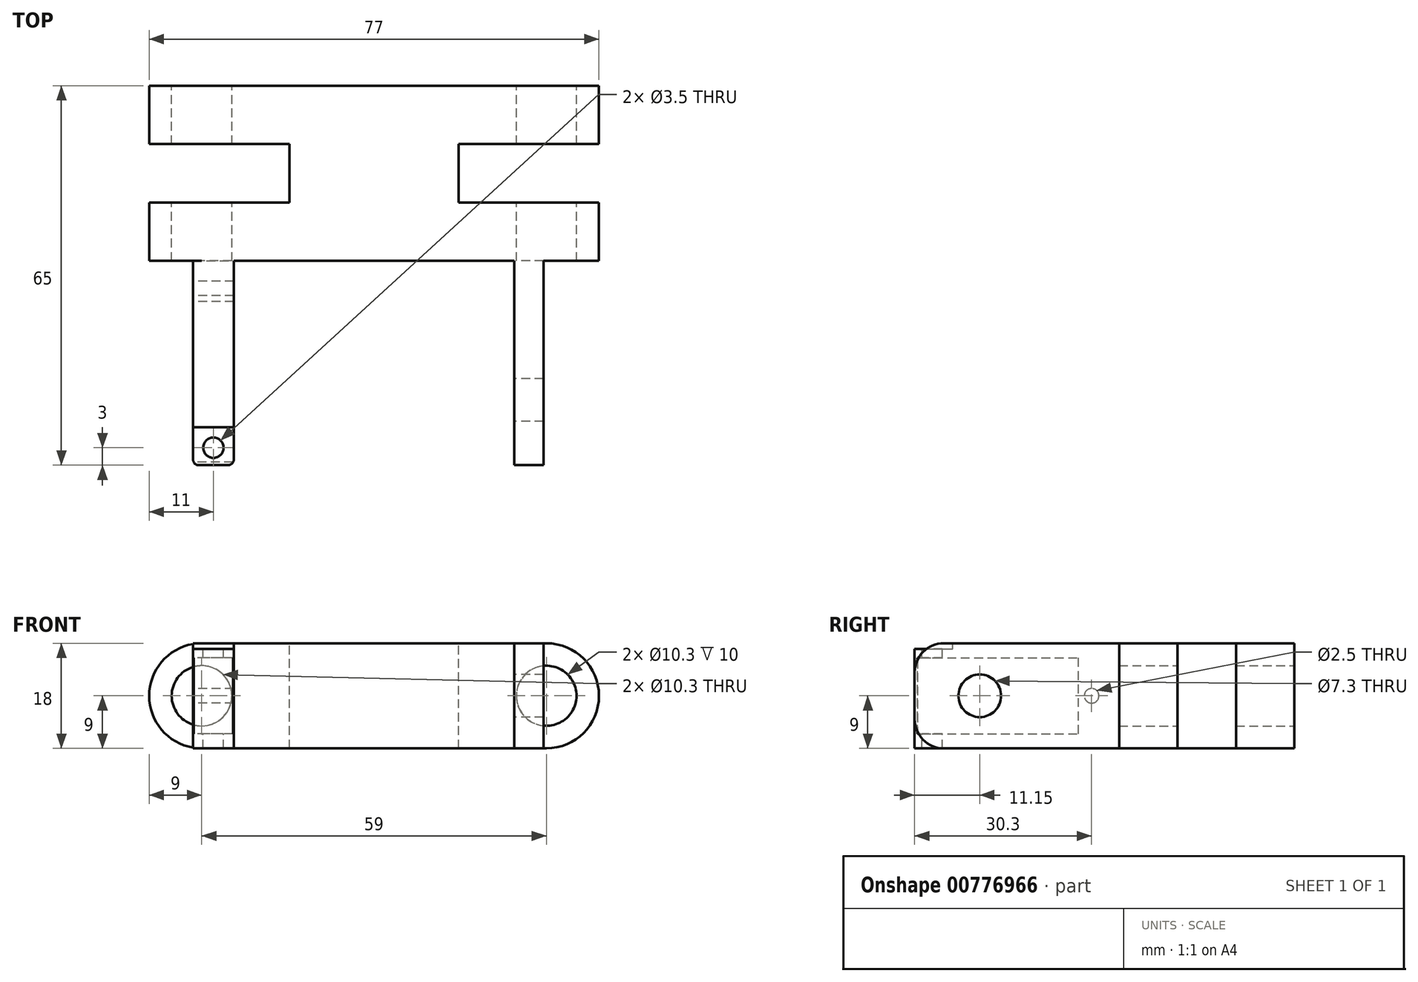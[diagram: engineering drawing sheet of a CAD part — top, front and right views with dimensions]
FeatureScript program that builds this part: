
annotation { "Feature Type Name" : "Feature", "Feature Type Description" : "" }
export const myFeature = defineFeature(function(context is Context, id is Id, definition is map)
    precondition{}
    {
        {
            var Q0;
            Q0=qCreatedBy(makeId("Front.planeOp"),FACE);
            var sketch = newSketch(context, id + "F0", { "sketchPlane" : qUnion([Q0])});
            skCircle(sketch, "E0", {"center": v(-59, 0) * mm, "radius": 5.15 * mm});
            skCircle(sketch, "E1", {"center": v(0, 0) * mm, "radius": 5.15 * mm});
            skCircle(sketch, "E2", {"center": v(-59, 0) * mm, "radius": 9 * mm});
            skCircle(sketch, "E3", {"center": v(0, 0) * mm, "radius": 9 * mm});
            skLineSegment(sketch, "E4", {"start": v(-59, 9) * mm, "end": v(0, 9) * mm});
            skLineSegment(sketch, "E5", {"start": v(-59, -9) * mm, "end": v(0, -9) * mm});
            skSolve(sketch);
        }
        {
            var Q0;
            Q0=qSketchRegion(id+"F0",true);
            extrude(context, id + "F1", {"entities" : qUnion([Q0]), "depth" : 30 * mm});
        }
        {
            var Q0;
            Q0=makeQuery(id+"F1.opExtrude","SWEPT_FACE",FACE,{"disambiguationData":[OSD([sQuery(id+"F0.wireOp",EDGE,"E4")])]});
            var sketch = newSketch(context, id + "F2", { "sketchPlane" : qUnion([Q0])});
            skLineSegment(sketch, "E6.bottom", {"start": v(-15, -10) * mm, "end": v(11.25, -10) * mm});
            skLineSegment(sketch, "E6.top", {"start": v(-15, -20) * mm, "end": v(11.25, -20) * mm});
            skLineSegment(sketch, "E6.left", {"start": v(-15, -10) * mm, "end": v(-15, -20) * mm});
            skLineSegment(sketch, "E6.right", {"start": v(11.25, -10) * mm, "end": v(11.25, -20) * mm});
            skLineSegment(sketch, "E7.bottom", {"start": v(-44, -10) * mm, "end": v(-74.23, -10) * mm});
            skLineSegment(sketch, "E7.top", {"start": v(-44, -20) * mm, "end": v(-74.23, -20) * mm});
            skLineSegment(sketch, "E7.left", {"start": v(-44, -10) * mm, "end": v(-44, -20) * mm});
            skLineSegment(sketch, "E7.right", {"start": v(-74.23, -10) * mm, "end": v(-74.23, -20) * mm});
            skSolve(sketch);
        }
        {
            var Q0;
            Q0=qSketchRegion(id+"F2",true);
            extrude(context, id + "F3", {"entities" : qUnion([Q0]), "operationType" : NewBodyOperationType.REMOVE, "oppositeDirection" : true, "depth" : 25 * mm});
        }
        {
            var Q0;
            Q0=makeQuery(id+"F1.opExtrude","CAP_FACE",FACE,{"disambiguationData":[OSD([sQuery(id+"F0.wireOp",EDGE,"E0"),sQuery(id+"F0.wireOp",EDGE,"E1"),sQuery(id+"F0.wireOp",EDGE,"E2"),sQuery(id+"F0.wireOp",EDGE,"E3"),sQuery(id+"F0.wireOp",EDGE,"E4"),sQuery(id+"F0.wireOp",EDGE,"E5")])],"isStart":false});
            var sketch = newSketch(context, id + "F4", { "sketchPlane" : qUnion([Q0])});
            skLineSegment(sketch, "E8.bottom", {"start": v(-5.5, 9) * mm, "end": v(-0.5, 9) * mm});
            skLineSegment(sketch, "E8.top", {"start": v(-5.5, -9) * mm, "end": v(-0.5, -9) * mm});
            skLineSegment(sketch, "E8.left", {"start": v(-5.5, 9) * mm, "end": v(-5.5, -9) * mm});
            skLineSegment(sketch, "E8.right", {"start": v(-0.5, 9) * mm, "end": v(-0.5, -9) * mm});
            skLineSegment(sketch, "E9.bottom", {"start": v(-60.5, 9) * mm, "end": v(-53.5, 9) * mm});
            skLineSegment(sketch, "E9.top", {"start": v(-60.5, -9) * mm, "end": v(-53.5, -9) * mm});
            skLineSegment(sketch, "E9.left", {"start": v(-60.5, 9) * mm, "end": v(-60.5, -9) * mm});
            skLineSegment(sketch, "E9.right", {"start": v(-53.5, 9) * mm, "end": v(-53.5, -9) * mm});
            skSolve(sketch);
        }
        {
            var Q0;
            Q0=qSketchRegion(id+"F4",true);
            extrude(context, id + "F5", {"entities" : qUnion([Q0]), "operationType" : NewBodyOperationType.ADD, "depth" : 35 * mm, "offsetDistance" : 25 * mm});
        }
        {
            var Q0;
            Q0=makeQuery(id+"F5.opExtrude","SWEPT_FACE",FACE,{"disambiguationData":[OSD([sQuery(id+"F4.wireOp",EDGE,"E9.left")])]});
            var sketch = newSketch(context, id + "F6", { "sketchPlane" : qUnion([Q0])});
            skLineSegment(sketch, "E10.bottom", {"start": v(64.5, 6.5) * mm, "end": v(37, 6.5) * mm});
            skLineSegment(sketch, "E10.top", {"start": v(64.5, -6.5) * mm, "end": v(37, -6.5) * mm});
            skLineSegment(sketch, "E10.left", {"start": v(64.5, 6.5) * mm, "end": v(64.5, -6.5) * mm});
            skLineSegment(sketch, "E10.right", {"start": v(37, 6.5) * mm, "end": v(37, -6.5) * mm});
            skPoint(sketch, "E11.centerSnap0", {"position": v(65, 0) * mm});
            skCircle(sketch, "E12", {"center": v(34.7, 0) * mm, "radius": 1.25 * mm});
            skSolve(sketch);
        }
        {
            var Q0;
            Q0=qSketchRegion(id+"F6",true);
            extrude(context, id + "F7", {"entities" : qUnion([Q0]), "operationType" : NewBodyOperationType.REMOVE, "oppositeDirection" : true, "depth" : 25 * mm, "offsetDistance" : 25 * mm});
        }
        {
            var Q0;
            Q0=makeQuery(id+"F5.opExtrude","SWEPT_FACE",FACE,{"disambiguationData":[OSD([sQuery(id+"F4.wireOp",EDGE,"E8.left")])]});
            var sketch = newSketch(context, id + "F8", { "sketchPlane" : qUnion([Q0])});
            skCircle(sketch, "E13", {"center": v(53.85, 0) * mm, "radius": 3.65 * mm});
            skPoint(sketch, "E13.centerSnap0", {"position": v(65, 0) * mm});
            skSolve(sketch);
        }
        {
            var Q0;
            Q0=qSketchRegion(id+"F8",true);
            extrude(context, id + "F9", {"entities" : qUnion([Q0]), "operationType" : NewBodyOperationType.REMOVE, "oppositeDirection" : true, "depth" : 25 * mm, "offsetDistance" : 25 * mm});
        }
        {
            var Q0;
            Q0=makeQuery(id+"F5.opExtrude","CAP_EDGE",EDGE,{"disambiguationData":[OSD([sQuery(id+"F4.wireOp",EDGE,"E8.bottom")])],"isStart":false});
            var Q1;
            Q1=makeQuery(id+"F5.opExtrude","CAP_EDGE",EDGE,{"disambiguationData":[OSD([sQuery(id+"F4.wireOp",EDGE,"E8.top")])],"isStart":false});
            fillet(context, id + "F10", {"entities" : qUnion([Q0, Q1]), "radius" : 5 * mm, "tangentPropagation" : true, "allowEdgeOverflow" : false});
        }
        {
            var Q0;
            Q0=makeQuery(id+"F5.boolean.opBoolean","MERGE",FACE,{"derivedFrom":[makeQuery(id+"F1.opExtrude","SWEPT_FACE",FACE,{"disambiguationData":[OSD([sQuery(id+"F0.wireOp",EDGE,"E4")])]}),makeQuery(id+"F5.opExtrude","SWEPT_FACE",FACE,{"disambiguationData":[OSD([sQuery(id+"F4.wireOp",EDGE,"E8.bottom")])]}),makeQuery(id+"F5.opExtrude","SWEPT_FACE",FACE,{"disambiguationData":[OSD([sQuery(id+"F4.wireOp",EDGE,"E9.bottom")])]})]});
            var sketch = newSketch(context, id + "F11", { "sketchPlane" : qUnion([Q0])});
            skCircle(sketch, "E14", {"center": v(-57, -62) * mm, "radius": 1.75 * mm});
            skPoint(sketch, "E14.centerSnap0", {"position": v(-57, -65) * mm});
            skSolve(sketch);
        }
        {
            var Q0;
            Q0=qSketchRegion(id+"F11",true);
            extrude(context, id + "F12", {"entities" : qUnion([Q0]), "operationType" : NewBodyOperationType.REMOVE, "oppositeDirection" : true, "depth" : 25 * mm, "offsetDistance" : 25 * mm});
        }
        {
            var Q0;
            Q0=makeQuery(id+"F5.boolean.opBoolean","MERGE",FACE,{"derivedFrom":[makeQuery(id+"F1.opExtrude","SWEPT_FACE",FACE,{"disambiguationData":[OSD([sQuery(id+"F0.wireOp",EDGE,"E4")])]}),makeQuery(id+"F5.opExtrude","SWEPT_FACE",FACE,{"disambiguationData":[OSD([sQuery(id+"F4.wireOp",EDGE,"E8.bottom")])]}),makeQuery(id+"F5.opExtrude","SWEPT_FACE",FACE,{"disambiguationData":[OSD([sQuery(id+"F4.wireOp",EDGE,"E9.bottom")])]})]});
            var sketch = newSketch(context, id + "F13", { "sketchPlane" : qUnion([Q0])});
            skLineSegment(sketch, "E15.bottom", {"start": v(-53.5, -65) * mm, "end": v(-60.5, -65) * mm});
            skLineSegment(sketch, "E15.top", {"start": v(-53.5, -58.5) * mm, "end": v(-60.5, -58.5) * mm});
            skLineSegment(sketch, "E15.left", {"start": v(-53.5, -65) * mm, "end": v(-53.5, -58.5) * mm});
            skLineSegment(sketch, "E15.right", {"start": v(-60.5, -65) * mm, "end": v(-60.5, -58.5) * mm});
            skSolve(sketch);
        }
        {
            var Q0;
            Q0=qSketchRegion(id+"F13",true);
            extrude(context, id + "F14", {"entities" : qUnion([Q0]), "operationType" : NewBodyOperationType.REMOVE, "oppositeDirection" : true, "depth" : 1 * mm, "offsetDistance" : 25 * mm});
        }
        {
            var Q0;
            Q0=makeQuery(id+"F5.opExtrude","CAP_EDGE",EDGE,{"disambiguationData":[OSD([sQuery(id+"F4.wireOp",EDGE,"E9.left")])],"isStart":false});
            var Q1;
            Q1=makeQuery(id+"F5.opExtrude","CAP_EDGE",EDGE,{"disambiguationData":[OSD([sQuery(id+"F4.wireOp",EDGE,"E9.right")])],"isStart":false});
            fillet(context, id + "F15", {"entities" : qUnion([Q0, Q1]), "radius" : 1 * mm, "tangentPropagation" : true, "allowEdgeOverflow" : false});
        }
    });
